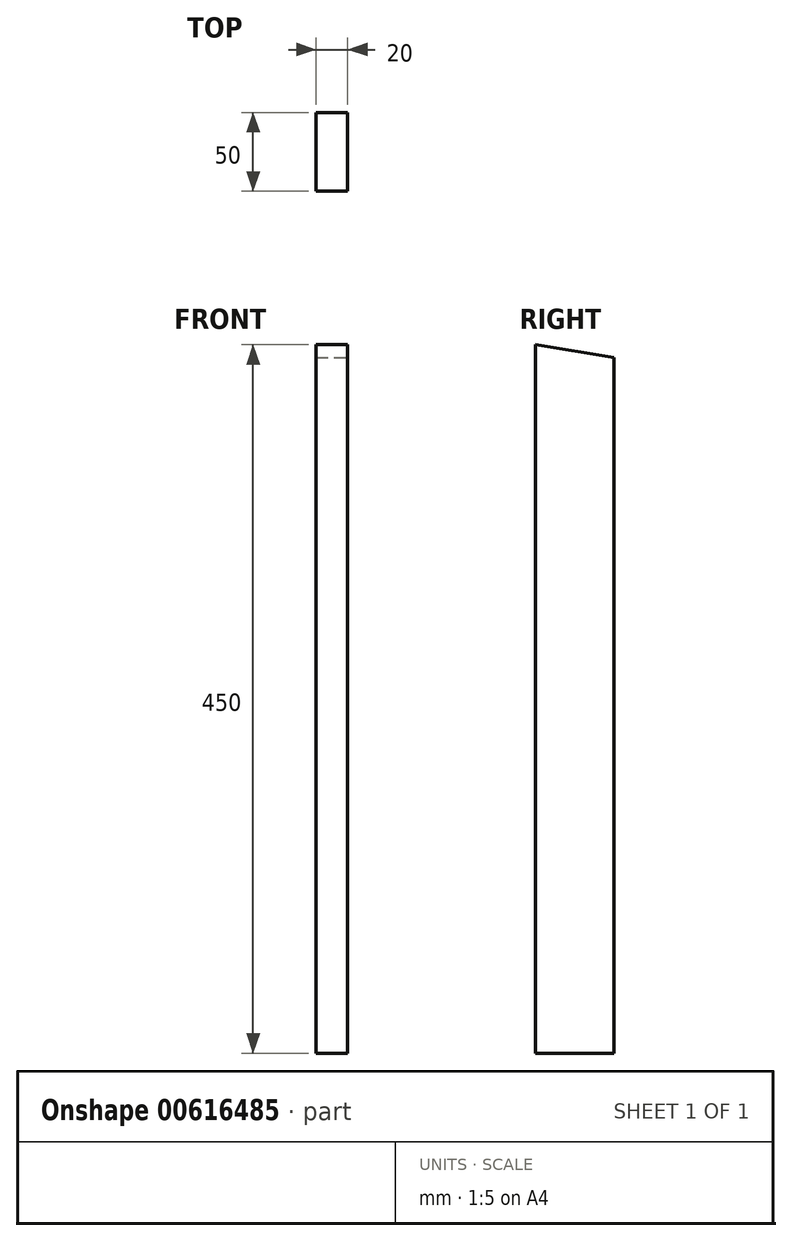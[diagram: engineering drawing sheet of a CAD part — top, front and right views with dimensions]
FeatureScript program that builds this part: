
annotation { "Feature Type Name" : "Feature", "Feature Type Description" : "" }
export const myFeature = defineFeature(function(context is Context, id is Id, definition is map)
    precondition{}
    {
        {
            var Q0;
            Q0=qCreatedBy(makeId("Front.planeOp"),FACE);
            var sketch = newSketch(context, id + "F0", { "sketchPlane" : qUnion([Q0])});
            skLineSegment(sketch, "E0.bottom", {"start": v(0, 0) * mm, "end": v(-20, 0) * mm});
            skLineSegment(sketch, "E0.top", {"start": v(0, 450) * mm, "end": v(-20, 450) * mm});
            skLineSegment(sketch, "E0.left", {"start": v(0, 0) * mm, "end": v(0, 450) * mm});
            skLineSegment(sketch, "E0.right", {"start": v(-20, 0) * mm, "end": v(-20, 450) * mm});
            skSolve(sketch);
        }
        {
            var Q0;
            Q0=makeQuery(id+"F0.imprint","IMPRINT",FACE,{"disambiguationData":[TD([[makeQuery(id+"F0.imprint","IMPRINT",EDGE,{"derivedFrom":sQuery(id+"F0.wireOp",EDGE,"E0.bottom")}),-1.0]])]});
            extrude(context, id + "F1", {"entities" : qUnion([Q0]), "depth" : 50 * mm, "offsetDistance" : 25 * mm});
        }
        {
            var Q0;
            Q0=makeQuery(id+"F1.opExtrude","SWEPT_FACE",FACE,{"disambiguationData":[OSD([sQuery(id+"F0.wireOp",EDGE,"E0.left")])]});
            var sketch = newSketch(context, id + "F2", { "sketchPlane" : qUnion([Q0])});
            skLineSegment(sketch, "E1", {"start": v(-50, 450) * mm, "end": v(0, 441.88) * mm});
            skLineSegment(sketch, "E2", {"start": v(0, 441.88) * mm, "end": v(0, 450) * mm});
            skLineSegment(sketch, "E3", {"start": v(0, 450) * mm, "end": v(-50, 450) * mm});
            skSolve(sketch);
        }
        {
            var Q0;
            Q0=makeQuery(id+"F2.imprint","IMPRINT",FACE,{"disambiguationData":[TD([[makeQuery(id+"F2.imprint","IMPRINT",EDGE,{"derivedFrom":sQuery(id+"F2.wireOp",EDGE,"E1")}),1.0]])]});
            extrude(context, id + "F3", {"entities" : qUnion([Q0]), "operationType" : NewBodyOperationType.REMOVE, "oppositeDirection" : true, "depth" : 25 * mm, "offsetDistance" : 25 * mm});
        }
    });
